# Revit family: WC-Wall Faced-Caroma Luna Close Coupled Suite1
name_source: partatom
category: Plumbing Fixtures
revit_build: Autodesk Revit 2014 (Build: 20130308_1515(x64)
units: mm (PartAtom-declared; Revit-internal decimal feet)

## types (1)
- Standard
    Assembly Code = D2010110
    CW Connection = Yes
    CWFU = 1.18
    Default Elevation = 0 mm  [stored 0 ft]
    Description = Caroma Luna Wall Faced Close Coupled Suite
    HW Connection = No
    Hardware = Metal-Chrome-Caroma
    Height_ANZRS = 794 mm
    Keynote = WC
    Length_ANZRS = 665 mm  [stored 2.18176 ft]
    Manufacturer = GWA Bathrooms & Kitchens
    Material_ANZRS = Porcelain-White-Caroma
    Model = 913500
    ModifiedIssue_ANZRS = 20150119.01 $
    Type Comments = White Only, S or P Trap, Back Inlet Cistern
    URL = http://www.caroma.com.au
    Vent Connection = No
    WELSRating_ANZRS = WELS 4 Star rated, 4.5/3L
    WFU = 1.18
    Waste Connection = Yes
    WasteOutlet_ANZRS = 0
    Width_ANZRS = 373 mm  [stored 1.22375 ft]

note: [stored X ft] marks values corroborated as IEEE doubles in the binary element streams (Revit-internal decimal feet)

## geometry (parser evidence)
native form markers: Blend x14, Sweep x2
no freeform markers — native parametric forms only
